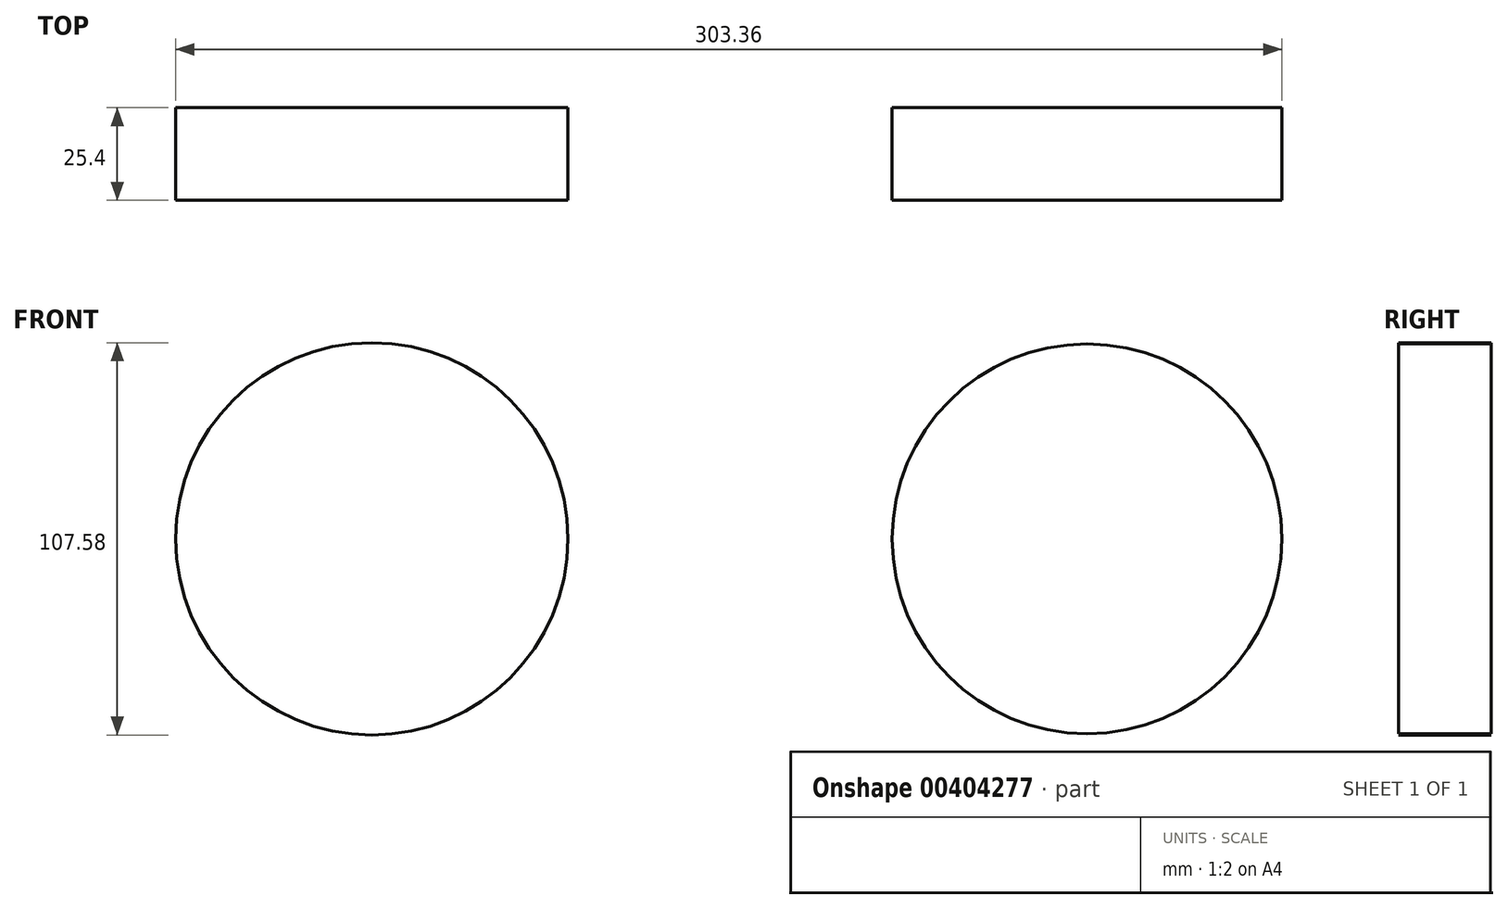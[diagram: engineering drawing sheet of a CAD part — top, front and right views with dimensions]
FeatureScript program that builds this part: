
annotation { "Feature Type Name" : "Feature", "Feature Type Description" : "" }
export const myFeature = defineFeature(function(context is Context, id is Id, definition is map)
    precondition{}
    {
        {
            var Q0;
            Q0=qCreatedBy(makeId("Front.planeOp"),FACE);
            var sketch = newSketch(context, id + "F0", { "sketchPlane" : qUnion([Q0])});
            skCircle(sketch, "E0", {"center": v(98.86, 0) * mm, "radius": 53.43 * mm});
            skCircle(sketch, "E1", {"center": v(-97.28, 0) * mm, "radius": 53.79 * mm});
            skSolve(sketch);
        }
        {
            var Q0;
            Q0=makeQuery(id+"F0.imprint","IMPRINT",FACE,{"disambiguationData":[TD([[makeQuery(id+"F0.imprint","IMPRINT",EDGE,{"derivedFrom":sQuery(id+"F0.wireOp",EDGE,"E0")}),1.0]])]});
            var Q1;
            Q1=makeQuery(id+"F0.imprint","IMPRINT",FACE,{"disambiguationData":[TD([[makeQuery(id+"F0.imprint","IMPRINT",EDGE,{"derivedFrom":sQuery(id+"F0.wireOp",EDGE,"E1")}),1.0]])]});
            extrude(context, id + "F1", {"entities" : qUnion([Q0, Q1]), "depth" : 25.4 * mm});
        }
    });
